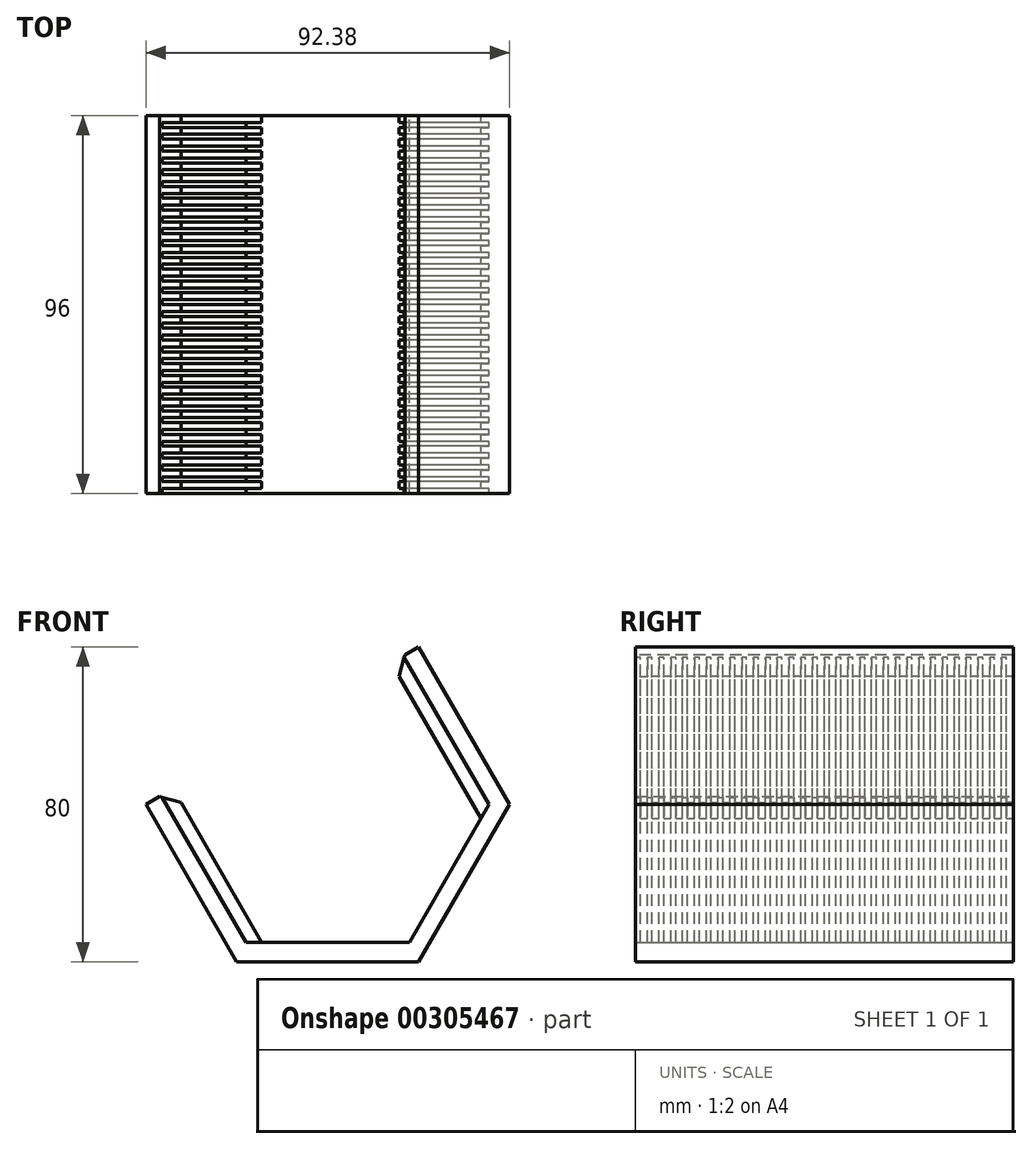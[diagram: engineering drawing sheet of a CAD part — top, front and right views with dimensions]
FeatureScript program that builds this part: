
annotation { "Feature Type Name" : "Feature", "Feature Type Description" : "" }
export const myFeature = defineFeature(function(context is Context, id is Id, definition is map)
    precondition{}
    {
        {
            var Q0;
            Q0=qCreatedBy(makeId("Front.planeOp"),FACE);
            var sketch = newSketch(context, id + "F0", { "sketchPlane" : qUnion([Q0])});
            skCircle(sketch, "E0.cCircle", {"center": v(0, 0) * mm, "radius": 46.19 * mm, "construction": true});
            skLineSegment(sketch, "E0.0", {"start": v(46.19, 0) * mm, "end": v(23.1, -40) * mm});
            skLineSegment(sketch, "E0.1", {"start": v(23.1, -40) * mm, "end": v(-23.1, -40) * mm});
            skLineSegment(sketch, "E0.2", {"start": v(-23.1, -40) * mm, "end": v(-46.19, 0) * mm});
            skLineSegment(sketch, "E0.3", {"start": v(-46.19, 0) * mm, "end": v(-23.1, 40) * mm});
            skLineSegment(sketch, "E0.4", {"start": v(-23.1, 40) * mm, "end": v(23.1, 40) * mm});
            skLineSegment(sketch, "E0.5", {"start": v(23.1, 40) * mm, "end": v(46.19, 0) * mm});
            skLineSegment(sketch, "E1.0", {"start": v(-21.36, -35) * mm, "end": v(-42.72, 2) * mm});
            skLineSegment(sketch, "E1.1", {"start": v(20.78, -35) * mm, "end": v(-21.36, -35) * mm});
            skLineSegment(sketch, "E1.2", {"start": v(41.28, 0.5) * mm, "end": v(20.78, -35) * mm});
            skLineSegment(sketch, "E1.3", {"start": v(19.63, 38) * mm, "end": v(41.28, 0.5) * mm});
            skLineSegment(sketch, "E2", {"start": v(-42.72, 2) * mm, "end": v(-46.19, 0) * mm});
            skLineSegment(sketch, "E3", {"start": v(19.63, 38) * mm, "end": v(23.1, 40) * mm});
            skSolve(sketch);
        }
        {
            var Q0;
            Q0=makeQuery(id+"F0.imprint","IMPRINT",FACE,{"disambiguationData":[TD([[makeQuery(id+"F0.imprint","IMPRINT",EDGE,{"derivedFrom":sQuery(id+"F0.wireOp",EDGE,"E0.0")}),-1.0]])]});
            extrude(context, id + "F1", {"entities" : qUnion([Q0]), "endBound" : BoundingType.SYMMETRIC, "depth" : 96 * mm});
        }
        {
            var Q0;
            Q0=makeQuery(id+"F1.opExtrude","SWEPT_FACE",FACE,{"disambiguationData":[OSD([sQuery(id+"F0.wireOp",EDGE,"E2")])]});
            var sketch = newSketch(context, id + "F2", { "sketchPlane" : qUnion([Q0])});
            skLineSegment(sketch, "E4", {"start": v(-32, 48) * mm, "end": v(-32, 46.25) * mm});
            skLineSegment(sketch, "E5", {"start": v(-32, 46.25) * mm, "end": v(-35.5, 46.25) * mm});
            skLineSegment(sketch, "E6", {"start": v(-35.5, 46.25) * mm, "end": v(-35.5, 45) * mm});
            skLineSegment(sketch, "E7", {"start": v(-36, 48) * mm, "end": v(-35.5, 48) * mm});
            skLineSegment(sketch, "E8", {"start": v(-35.5, 48) * mm, "end": v(-32, 48) * mm});
            skLineSegment(sketch, "E9.0.1.0", {"start": v(-35.5, 45) * mm, "end": v(-32, 45) * mm});
            skLineSegment(sketch, "E9.0.1.1", {"start": v(-32, 45) * mm, "end": v(-32, 43.25) * mm});
            skLineSegment(sketch, "E9.0.1.2", {"start": v(-32, 43.25) * mm, "end": v(-35.5, 43.25) * mm});
            skLineSegment(sketch, "E9.0.1.3", {"start": v(-35.5, 43.25) * mm, "end": v(-35.5, 42) * mm});
            skLineSegment(sketch, "E9.0.2.0", {"start": v(-35.5, 42) * mm, "end": v(-32, 42) * mm});
            skLineSegment(sketch, "E9.0.2.1", {"start": v(-32, 42) * mm, "end": v(-32, 40.25) * mm});
            skLineSegment(sketch, "E9.0.2.2", {"start": v(-32, 40.25) * mm, "end": v(-35.5, 40.25) * mm});
            skLineSegment(sketch, "E9.0.2.3", {"start": v(-35.5, 40.25) * mm, "end": v(-35.5, 39) * mm});
            skLineSegment(sketch, "E9.0.3.0", {"start": v(-35.5, 39) * mm, "end": v(-32, 39) * mm});
            skLineSegment(sketch, "E9.0.3.1", {"start": v(-32, 39) * mm, "end": v(-32, 37.25) * mm});
            skLineSegment(sketch, "E9.0.3.2", {"start": v(-32, 37.25) * mm, "end": v(-35.5, 37.25) * mm});
            skLineSegment(sketch, "E9.0.3.3", {"start": v(-35.5, 37.25) * mm, "end": v(-35.5, 36) * mm});
            skLineSegment(sketch, "E9.0.4.0", {"start": v(-35.5, 36) * mm, "end": v(-32, 36) * mm});
            skLineSegment(sketch, "E9.0.4.1", {"start": v(-32, 36) * mm, "end": v(-32, 34.25) * mm});
            skLineSegment(sketch, "E9.0.4.2", {"start": v(-32, 34.25) * mm, "end": v(-35.5, 34.25) * mm});
            skLineSegment(sketch, "E9.0.4.3", {"start": v(-35.5, 34.25) * mm, "end": v(-35.5, 33) * mm});
            skLineSegment(sketch, "E9.0.5.0", {"start": v(-35.5, 33) * mm, "end": v(-32, 33) * mm});
            skLineSegment(sketch, "E9.0.5.1", {"start": v(-32, 33) * mm, "end": v(-32, 31.25) * mm});
            skLineSegment(sketch, "E9.0.5.2", {"start": v(-32, 31.25) * mm, "end": v(-35.5, 31.25) * mm});
            skLineSegment(sketch, "E9.0.5.3", {"start": v(-35.5, 31.25) * mm, "end": v(-35.5, 30) * mm});
            skLineSegment(sketch, "E9.0.6.0", {"start": v(-35.5, 30) * mm, "end": v(-32, 30) * mm});
            skLineSegment(sketch, "E9.0.6.1", {"start": v(-32, 30) * mm, "end": v(-32, 28.25) * mm});
            skLineSegment(sketch, "E9.0.6.2", {"start": v(-32, 28.25) * mm, "end": v(-35.5, 28.25) * mm});
            skLineSegment(sketch, "E9.0.6.3", {"start": v(-35.5, 28.25) * mm, "end": v(-35.5, 27) * mm});
            skLineSegment(sketch, "E9.0.7.0", {"start": v(-35.5, 27) * mm, "end": v(-32, 27) * mm});
            skLineSegment(sketch, "E9.0.7.1", {"start": v(-32, 27) * mm, "end": v(-32, 25.25) * mm});
            skLineSegment(sketch, "E9.0.7.2", {"start": v(-32, 25.25) * mm, "end": v(-35.5, 25.25) * mm});
            skLineSegment(sketch, "E9.0.7.3", {"start": v(-35.5, 25.25) * mm, "end": v(-35.5, 24) * mm});
            skLineSegment(sketch, "E9.0.8.0", {"start": v(-35.5, 24) * mm, "end": v(-32, 24) * mm});
            skLineSegment(sketch, "E9.0.8.1", {"start": v(-32, 24) * mm, "end": v(-32, 22.25) * mm});
            skLineSegment(sketch, "E9.0.8.2", {"start": v(-32, 22.25) * mm, "end": v(-35.5, 22.25) * mm});
            skLineSegment(sketch, "E9.0.8.3", {"start": v(-35.5, 22.25) * mm, "end": v(-35.5, 21) * mm});
            skLineSegment(sketch, "E9.0.9.0", {"start": v(-35.5, 21) * mm, "end": v(-32, 21) * mm});
            skLineSegment(sketch, "E9.0.9.1", {"start": v(-32, 21) * mm, "end": v(-32, 19.25) * mm});
            skLineSegment(sketch, "E9.0.9.2", {"start": v(-32, 19.25) * mm, "end": v(-35.5, 19.25) * mm});
            skLineSegment(sketch, "E9.0.9.3", {"start": v(-35.5, 19.25) * mm, "end": v(-35.5, 18) * mm});
            skLineSegment(sketch, "E9.0.10.0", {"start": v(-35.5, 18) * mm, "end": v(-32, 18) * mm});
            skLineSegment(sketch, "E9.0.10.1", {"start": v(-32, 18) * mm, "end": v(-32, 16.25) * mm});
            skLineSegment(sketch, "E9.0.10.2", {"start": v(-32, 16.25) * mm, "end": v(-35.5, 16.25) * mm});
            skLineSegment(sketch, "E9.0.10.3", {"start": v(-35.5, 16.25) * mm, "end": v(-35.5, 15) * mm});
            skLineSegment(sketch, "E9.0.11.0", {"start": v(-35.5, 15) * mm, "end": v(-32, 15) * mm});
            skLineSegment(sketch, "E9.0.11.1", {"start": v(-32, 15) * mm, "end": v(-32, 13.25) * mm});
            skLineSegment(sketch, "E9.0.11.2", {"start": v(-32, 13.25) * mm, "end": v(-35.5, 13.25) * mm});
            skLineSegment(sketch, "E9.0.11.3", {"start": v(-35.5, 13.25) * mm, "end": v(-35.5, 12) * mm});
            skLineSegment(sketch, "E9.0.12.0", {"start": v(-35.5, 12) * mm, "end": v(-32, 12) * mm});
            skLineSegment(sketch, "E9.0.12.1", {"start": v(-32, 12) * mm, "end": v(-32, 10.25) * mm});
            skLineSegment(sketch, "E9.0.12.2", {"start": v(-32, 10.25) * mm, "end": v(-35.5, 10.25) * mm});
            skLineSegment(sketch, "E9.0.12.3", {"start": v(-35.5, 10.25) * mm, "end": v(-35.5, 9) * mm});
            skLineSegment(sketch, "E9.0.13.0", {"start": v(-35.5, 9) * mm, "end": v(-32, 9) * mm});
            skLineSegment(sketch, "E9.0.13.1", {"start": v(-32, 9) * mm, "end": v(-32, 7.25) * mm});
            skLineSegment(sketch, "E9.0.13.2", {"start": v(-32, 7.25) * mm, "end": v(-35.5, 7.25) * mm});
            skLineSegment(sketch, "E9.0.13.3", {"start": v(-35.5, 7.25) * mm, "end": v(-35.5, 6) * mm});
            skLineSegment(sketch, "E9.0.14.0", {"start": v(-35.5, 6) * mm, "end": v(-32, 6) * mm});
            skLineSegment(sketch, "E9.0.14.1", {"start": v(-32, 6) * mm, "end": v(-32, 4.25) * mm});
            skLineSegment(sketch, "E9.0.14.2", {"start": v(-32, 4.25) * mm, "end": v(-35.5, 4.25) * mm});
            skLineSegment(sketch, "E9.0.14.3", {"start": v(-35.5, 4.25) * mm, "end": v(-35.5, 3) * mm});
            skLineSegment(sketch, "E9.0.15.0", {"start": v(-35.5, 3) * mm, "end": v(-32, 3) * mm});
            skLineSegment(sketch, "E9.0.15.1", {"start": v(-32, 3) * mm, "end": v(-32, 1.25) * mm});
            skLineSegment(sketch, "E9.0.15.2", {"start": v(-32, 1.25) * mm, "end": v(-35.5, 1.25) * mm});
            skLineSegment(sketch, "E9.0.15.3", {"start": v(-35.5, 1.25) * mm, "end": v(-35.5, 0) * mm});
            skLineSegment(sketch, "E9.0.16.0", {"start": v(-35.5, 0) * mm, "end": v(-32, 0) * mm});
            skLineSegment(sketch, "E9.0.16.1", {"start": v(-32, 0) * mm, "end": v(-32, -1.75) * mm});
            skLineSegment(sketch, "E9.0.16.2", {"start": v(-32, -1.75) * mm, "end": v(-35.5, -1.75) * mm});
            skLineSegment(sketch, "E9.0.16.3", {"start": v(-35.5, -1.75) * mm, "end": v(-35.5, -3) * mm});
            skLineSegment(sketch, "E9.0.17.0", {"start": v(-35.5, -3) * mm, "end": v(-32, -3) * mm});
            skLineSegment(sketch, "E9.0.17.1", {"start": v(-32, -3) * mm, "end": v(-32, -4.75) * mm});
            skLineSegment(sketch, "E9.0.17.2", {"start": v(-32, -4.75) * mm, "end": v(-35.5, -4.75) * mm});
            skLineSegment(sketch, "E9.0.17.3", {"start": v(-35.5, -4.75) * mm, "end": v(-35.5, -6) * mm});
            skLineSegment(sketch, "E9.0.18.0", {"start": v(-35.5, -6) * mm, "end": v(-32, -6) * mm});
            skLineSegment(sketch, "E9.0.18.1", {"start": v(-32, -6) * mm, "end": v(-32, -7.75) * mm});
            skLineSegment(sketch, "E9.0.18.2", {"start": v(-32, -7.75) * mm, "end": v(-35.5, -7.75) * mm});
            skLineSegment(sketch, "E9.0.18.3", {"start": v(-35.5, -7.75) * mm, "end": v(-35.5, -9) * mm});
            skLineSegment(sketch, "E9.0.19.0", {"start": v(-35.5, -9) * mm, "end": v(-32, -9) * mm});
            skLineSegment(sketch, "E9.0.19.1", {"start": v(-32, -9) * mm, "end": v(-32, -10.75) * mm});
            skLineSegment(sketch, "E9.0.19.2", {"start": v(-32, -10.75) * mm, "end": v(-35.5, -10.75) * mm});
            skLineSegment(sketch, "E9.0.19.3", {"start": v(-35.5, -10.75) * mm, "end": v(-35.5, -12) * mm});
            skLineSegment(sketch, "E9.direction1", {"start": v(-35.5, 48) * mm, "end": v(-25.3, 48) * mm, "construction": true});
            skLineSegment(sketch, "E9.direction2", {"start": v(-35.5, 48) * mm, "end": v(-35.5, 45) * mm, "construction": true});
            skLineSegment(sketch, "E10.0.0.20", {"start": v(-35.5, -12) * mm, "end": v(-32, -12) * mm});
            skLineSegment(sketch, "E10.3.0.20", {"start": v(-32, -12) * mm, "end": v(-32, -13.75) * mm});
            skLineSegment(sketch, "E10.6.0.20", {"start": v(-32, -13.75) * mm, "end": v(-35.5, -13.75) * mm});
            skLineSegment(sketch, "E10.9.0.20", {"start": v(-35.5, -13.75) * mm, "end": v(-35.5, -15) * mm});
            skLineSegment(sketch, "E10.0.0.21", {"start": v(-35.5, -15) * mm, "end": v(-32, -15) * mm});
            skLineSegment(sketch, "E10.3.0.21", {"start": v(-32, -15) * mm, "end": v(-32, -16.75) * mm});
            skLineSegment(sketch, "E10.6.0.21", {"start": v(-32, -16.75) * mm, "end": v(-35.5, -16.75) * mm});
            skLineSegment(sketch, "E10.9.0.21", {"start": v(-35.5, -16.75) * mm, "end": v(-35.5, -18) * mm});
            skLineSegment(sketch, "E10.0.0.22", {"start": v(-35.5, -18) * mm, "end": v(-32, -18) * mm});
            skLineSegment(sketch, "E10.3.0.22", {"start": v(-32, -18) * mm, "end": v(-32, -19.75) * mm});
            skLineSegment(sketch, "E10.6.0.22", {"start": v(-32, -19.75) * mm, "end": v(-35.5, -19.75) * mm});
            skLineSegment(sketch, "E10.9.0.22", {"start": v(-35.5, -19.75) * mm, "end": v(-35.5, -21) * mm});
            skLineSegment(sketch, "E10.0.0.23", {"start": v(-35.5, -21) * mm, "end": v(-32, -21) * mm});
            skLineSegment(sketch, "E10.3.0.23", {"start": v(-32, -21) * mm, "end": v(-32, -22.75) * mm});
            skLineSegment(sketch, "E10.6.0.23", {"start": v(-32, -22.75) * mm, "end": v(-35.5, -22.75) * mm});
            skLineSegment(sketch, "E10.9.0.23", {"start": v(-35.5, -22.75) * mm, "end": v(-35.5, -24) * mm});
            skLineSegment(sketch, "E10.0.0.24", {"start": v(-35.5, -24) * mm, "end": v(-32, -24) * mm});
            skLineSegment(sketch, "E10.3.0.24", {"start": v(-32, -24) * mm, "end": v(-32, -25.75) * mm});
            skLineSegment(sketch, "E10.6.0.24", {"start": v(-32, -25.75) * mm, "end": v(-35.5, -25.75) * mm});
            skLineSegment(sketch, "E10.9.0.24", {"start": v(-35.5, -25.75) * mm, "end": v(-35.5, -27) * mm});
            skLineSegment(sketch, "E10.0.0.25", {"start": v(-35.5, -27) * mm, "end": v(-32, -27) * mm});
            skLineSegment(sketch, "E10.3.0.25", {"start": v(-32, -27) * mm, "end": v(-32, -28.75) * mm});
            skLineSegment(sketch, "E10.6.0.25", {"start": v(-32, -28.75) * mm, "end": v(-35.5, -28.75) * mm});
            skLineSegment(sketch, "E10.9.0.25", {"start": v(-35.5, -28.75) * mm, "end": v(-35.5, -30) * mm});
            skLineSegment(sketch, "E10.0.0.26", {"start": v(-35.5, -30) * mm, "end": v(-32, -30) * mm});
            skLineSegment(sketch, "E10.3.0.26", {"start": v(-32, -30) * mm, "end": v(-32, -31.75) * mm});
            skLineSegment(sketch, "E10.6.0.26", {"start": v(-32, -31.75) * mm, "end": v(-35.5, -31.75) * mm});
            skLineSegment(sketch, "E10.9.0.26", {"start": v(-35.5, -31.75) * mm, "end": v(-35.5, -33) * mm});
            skLineSegment(sketch, "E10.0.0.27", {"start": v(-35.5, -33) * mm, "end": v(-32, -33) * mm});
            skLineSegment(sketch, "E10.3.0.27", {"start": v(-32, -33) * mm, "end": v(-32, -34.75) * mm});
            skLineSegment(sketch, "E10.6.0.27", {"start": v(-32, -34.75) * mm, "end": v(-35.5, -34.75) * mm});
            skLineSegment(sketch, "E10.9.0.27", {"start": v(-35.5, -34.75) * mm, "end": v(-35.5, -36) * mm});
            skLineSegment(sketch, "E10.0.0.28", {"start": v(-35.5, -36) * mm, "end": v(-32, -36) * mm});
            skLineSegment(sketch, "E10.3.0.28", {"start": v(-32, -36) * mm, "end": v(-32, -37.75) * mm});
            skLineSegment(sketch, "E10.6.0.28", {"start": v(-32, -37.75) * mm, "end": v(-35.5, -37.75) * mm});
            skLineSegment(sketch, "E10.9.0.28", {"start": v(-35.5, -37.75) * mm, "end": v(-35.5, -39) * mm});
            skLineSegment(sketch, "E10.0.0.29", {"start": v(-35.5, -39) * mm, "end": v(-32, -39) * mm});
            skLineSegment(sketch, "E10.3.0.29", {"start": v(-32, -39) * mm, "end": v(-32, -40.75) * mm});
            skLineSegment(sketch, "E10.6.0.29", {"start": v(-32, -40.75) * mm, "end": v(-35.5, -40.75) * mm});
            skLineSegment(sketch, "E10.9.0.29", {"start": v(-35.5, -40.75) * mm, "end": v(-35.5, -42) * mm});
            skLineSegment(sketch, "E11.0.0.30", {"start": v(-35.5, -42) * mm, "end": v(-32, -42) * mm});
            skLineSegment(sketch, "E11.3.0.30", {"start": v(-32, -42) * mm, "end": v(-32, -43.75) * mm});
            skLineSegment(sketch, "E11.6.0.30", {"start": v(-32, -43.75) * mm, "end": v(-35.5, -43.75) * mm});
            skLineSegment(sketch, "E11.9.0.30", {"start": v(-35.5, -43.75) * mm, "end": v(-35.5, -45) * mm});
            skLineSegment(sketch, "E11.0.0.31", {"start": v(-35.5, -45) * mm, "end": v(-32, -45) * mm});
            skLineSegment(sketch, "E11.3.0.31", {"start": v(-32, -45) * mm, "end": v(-32, -46.75) * mm});
            skLineSegment(sketch, "E11.6.0.31", {"start": v(-32, -46.75) * mm, "end": v(-35.5, -46.75) * mm});
            skLineSegment(sketch, "E11.9.0.31", {"start": v(-35.5, -46.75) * mm, "end": v(-35.5, -48) * mm});
            skLineSegment(sketch, "E12", {"start": v(-35.5, -48) * mm, "end": v(-36, -48) * mm});
            skSolve(sketch);
        }
        {
            var Q0;
            Q0 = qSketchRegion(id + "F2", true);
            var Q1;
            Q1=makeQuery(id+"F2.imprint","IMPRINT",FACE,{"disambiguationData":[TD([[makeQuery(id+"F2.imprint","IMPRINT",EDGE,{"derivedFrom":sQuery(id+"F2.wireOp",EDGE,"E4")}),-1.0]])]});
            extrude(context, id + "F3", {"entities" : qUnion([Q0, Q1]), "operationType" : NewBodyOperationType.ADD, "oppositeDirection" : true, "depth" : 46 * mm});
        }
        {
            var Q0;
            Q0=makeQuery(id+"F1.opExtrude","SWEPT_FACE",FACE,{"disambiguationData":[OSD([sQuery(id+"F0.wireOp",EDGE,"E3")])]});
            var sketch = newSketch(context, id + "F4", { "sketchPlane" : qUnion([Q0])});
            skLineSegment(sketch, "E13", {"start": v(36, 48) * mm, "end": v(35.5, 48) * mm});
            skLineSegment(sketch, "E14", {"start": v(35.5, 48) * mm, "end": v(32, 48) * mm});
            skLineSegment(sketch, "E15", {"start": v(32, 48) * mm, "end": v(32, 46.25) * mm});
            skLineSegment(sketch, "E16", {"start": v(32, 46.25) * mm, "end": v(35.5, 46.25) * mm});
            skLineSegment(sketch, "E17", {"start": v(35.5, 46.25) * mm, "end": v(35.5, 45) * mm});
            skLineSegment(sketch, "E18.0.1.0", {"start": v(35.5, 45) * mm, "end": v(32, 45) * mm});
            skLineSegment(sketch, "E18.0.1.1", {"start": v(32, 45) * mm, "end": v(32, 43.25) * mm});
            skLineSegment(sketch, "E18.0.1.2", {"start": v(32, 43.25) * mm, "end": v(35.5, 43.25) * mm});
            skLineSegment(sketch, "E18.0.1.3", {"start": v(35.5, 43.25) * mm, "end": v(35.5, 42) * mm});
            skLineSegment(sketch, "E18.0.2.0", {"start": v(35.5, 42) * mm, "end": v(32, 42) * mm});
            skLineSegment(sketch, "E18.0.2.1", {"start": v(32, 42) * mm, "end": v(32, 40.25) * mm});
            skLineSegment(sketch, "E18.0.2.2", {"start": v(32, 40.25) * mm, "end": v(35.5, 40.25) * mm});
            skLineSegment(sketch, "E18.0.2.3", {"start": v(35.5, 40.25) * mm, "end": v(35.5, 39) * mm});
            skLineSegment(sketch, "E18.0.3.0", {"start": v(35.5, 39) * mm, "end": v(32, 39) * mm});
            skLineSegment(sketch, "E18.0.3.1", {"start": v(32, 39) * mm, "end": v(32, 37.25) * mm});
            skLineSegment(sketch, "E18.0.3.2", {"start": v(32, 37.25) * mm, "end": v(35.5, 37.25) * mm});
            skLineSegment(sketch, "E18.0.3.3", {"start": v(35.5, 37.25) * mm, "end": v(35.5, 36) * mm});
            skLineSegment(sketch, "E18.0.4.0", {"start": v(35.5, 36) * mm, "end": v(32, 36) * mm});
            skLineSegment(sketch, "E18.0.4.1", {"start": v(32, 36) * mm, "end": v(32, 34.25) * mm});
            skLineSegment(sketch, "E18.0.4.2", {"start": v(32, 34.25) * mm, "end": v(35.5, 34.25) * mm});
            skLineSegment(sketch, "E18.0.4.3", {"start": v(35.5, 34.25) * mm, "end": v(35.5, 33) * mm});
            skLineSegment(sketch, "E18.0.5.0", {"start": v(35.5, 33) * mm, "end": v(32, 33) * mm});
            skLineSegment(sketch, "E18.0.5.1", {"start": v(32, 33) * mm, "end": v(32, 31.25) * mm});
            skLineSegment(sketch, "E18.0.5.2", {"start": v(32, 31.25) * mm, "end": v(35.5, 31.25) * mm});
            skLineSegment(sketch, "E18.0.5.3", {"start": v(35.5, 31.25) * mm, "end": v(35.5, 30) * mm});
            skLineSegment(sketch, "E18.0.6.0", {"start": v(35.5, 30) * mm, "end": v(32, 30) * mm});
            skLineSegment(sketch, "E18.0.6.1", {"start": v(32, 30) * mm, "end": v(32, 28.25) * mm});
            skLineSegment(sketch, "E18.0.6.2", {"start": v(32, 28.25) * mm, "end": v(35.5, 28.25) * mm});
            skLineSegment(sketch, "E18.0.6.3", {"start": v(35.5, 28.25) * mm, "end": v(35.5, 27) * mm});
            skLineSegment(sketch, "E18.0.7.0", {"start": v(35.5, 27) * mm, "end": v(32, 27) * mm});
            skLineSegment(sketch, "E18.0.7.1", {"start": v(32, 27) * mm, "end": v(32, 25.25) * mm});
            skLineSegment(sketch, "E18.0.7.2", {"start": v(32, 25.25) * mm, "end": v(35.5, 25.25) * mm});
            skLineSegment(sketch, "E18.0.7.3", {"start": v(35.5, 25.25) * mm, "end": v(35.5, 24) * mm});
            skLineSegment(sketch, "E18.0.8.0", {"start": v(35.5, 24) * mm, "end": v(32, 24) * mm});
            skLineSegment(sketch, "E18.0.8.1", {"start": v(32, 24) * mm, "end": v(32, 22.25) * mm});
            skLineSegment(sketch, "E18.0.8.2", {"start": v(32, 22.25) * mm, "end": v(35.5, 22.25) * mm});
            skLineSegment(sketch, "E18.0.8.3", {"start": v(35.5, 22.25) * mm, "end": v(35.5, 21) * mm});
            skLineSegment(sketch, "E18.0.9.0", {"start": v(35.5, 21) * mm, "end": v(32, 21) * mm});
            skLineSegment(sketch, "E18.0.9.1", {"start": v(32, 21) * mm, "end": v(32, 19.25) * mm});
            skLineSegment(sketch, "E18.0.9.2", {"start": v(32, 19.25) * mm, "end": v(35.5, 19.25) * mm});
            skLineSegment(sketch, "E18.0.9.3", {"start": v(35.5, 19.25) * mm, "end": v(35.5, 18) * mm});
            skLineSegment(sketch, "E18.0.10.0", {"start": v(35.5, 18) * mm, "end": v(32, 18) * mm});
            skLineSegment(sketch, "E18.0.10.1", {"start": v(32, 18) * mm, "end": v(32, 16.25) * mm});
            skLineSegment(sketch, "E18.0.10.2", {"start": v(32, 16.25) * mm, "end": v(35.5, 16.25) * mm});
            skLineSegment(sketch, "E18.0.10.3", {"start": v(35.5, 16.25) * mm, "end": v(35.5, 15) * mm});
            skLineSegment(sketch, "E18.0.11.0", {"start": v(35.5, 15) * mm, "end": v(32, 15) * mm});
            skLineSegment(sketch, "E18.0.11.1", {"start": v(32, 15) * mm, "end": v(32, 13.25) * mm});
            skLineSegment(sketch, "E18.0.11.2", {"start": v(32, 13.25) * mm, "end": v(35.5, 13.25) * mm});
            skLineSegment(sketch, "E18.0.11.3", {"start": v(35.5, 13.25) * mm, "end": v(35.5, 12) * mm});
            skLineSegment(sketch, "E18.0.12.0", {"start": v(35.5, 12) * mm, "end": v(32, 12) * mm});
            skLineSegment(sketch, "E18.0.12.1", {"start": v(32, 12) * mm, "end": v(32, 10.25) * mm});
            skLineSegment(sketch, "E18.0.12.2", {"start": v(32, 10.25) * mm, "end": v(35.5, 10.25) * mm});
            skLineSegment(sketch, "E18.0.12.3", {"start": v(35.5, 10.25) * mm, "end": v(35.5, 9) * mm});
            skLineSegment(sketch, "E18.0.13.0", {"start": v(35.5, 9) * mm, "end": v(32, 9) * mm});
            skLineSegment(sketch, "E18.0.13.1", {"start": v(32, 9) * mm, "end": v(32, 7.25) * mm});
            skLineSegment(sketch, "E18.0.13.2", {"start": v(32, 7.25) * mm, "end": v(35.5, 7.25) * mm});
            skLineSegment(sketch, "E18.0.13.3", {"start": v(35.5, 7.25) * mm, "end": v(35.5, 6) * mm});
            skLineSegment(sketch, "E18.0.14.0", {"start": v(35.5, 6) * mm, "end": v(32, 6) * mm});
            skLineSegment(sketch, "E18.0.14.1", {"start": v(32, 6) * mm, "end": v(32, 4.25) * mm});
            skLineSegment(sketch, "E18.0.14.2", {"start": v(32, 4.25) * mm, "end": v(35.5, 4.25) * mm});
            skLineSegment(sketch, "E18.0.14.3", {"start": v(35.5, 4.25) * mm, "end": v(35.5, 3) * mm});
            skLineSegment(sketch, "E18.0.15.0", {"start": v(35.5, 3) * mm, "end": v(32, 3) * mm});
            skLineSegment(sketch, "E18.0.15.1", {"start": v(32, 3) * mm, "end": v(32, 1.25) * mm});
            skLineSegment(sketch, "E18.0.15.2", {"start": v(32, 1.25) * mm, "end": v(35.5, 1.25) * mm});
            skLineSegment(sketch, "E18.0.15.3", {"start": v(35.5, 1.25) * mm, "end": v(35.5, 0) * mm});
            skLineSegment(sketch, "E18.0.16.0", {"start": v(35.5, 0) * mm, "end": v(32, 0) * mm});
            skLineSegment(sketch, "E18.0.16.1", {"start": v(32, 0) * mm, "end": v(32, -1.75) * mm});
            skLineSegment(sketch, "E18.0.16.2", {"start": v(32, -1.75) * mm, "end": v(35.5, -1.75) * mm});
            skLineSegment(sketch, "E18.0.16.3", {"start": v(35.5, -1.75) * mm, "end": v(35.5, -3) * mm});
            skLineSegment(sketch, "E18.0.17.0", {"start": v(35.5, -3) * mm, "end": v(32, -3) * mm});
            skLineSegment(sketch, "E18.0.17.1", {"start": v(32, -3) * mm, "end": v(32, -4.75) * mm});
            skLineSegment(sketch, "E18.0.17.2", {"start": v(32, -4.75) * mm, "end": v(35.5, -4.75) * mm});
            skLineSegment(sketch, "E18.0.17.3", {"start": v(35.5, -4.75) * mm, "end": v(35.5, -6) * mm});
            skLineSegment(sketch, "E18.0.18.0", {"start": v(35.5, -6) * mm, "end": v(32, -6) * mm});
            skLineSegment(sketch, "E18.0.18.1", {"start": v(32, -6) * mm, "end": v(32, -7.75) * mm});
            skLineSegment(sketch, "E18.0.18.2", {"start": v(32, -7.75) * mm, "end": v(35.5, -7.75) * mm});
            skLineSegment(sketch, "E18.0.18.3", {"start": v(35.5, -7.75) * mm, "end": v(35.5, -9) * mm});
            skLineSegment(sketch, "E18.0.19.0", {"start": v(35.5, -9) * mm, "end": v(32, -9) * mm});
            skLineSegment(sketch, "E18.0.19.1", {"start": v(32, -9) * mm, "end": v(32, -10.75) * mm});
            skLineSegment(sketch, "E18.0.19.2", {"start": v(32, -10.75) * mm, "end": v(35.5, -10.75) * mm});
            skLineSegment(sketch, "E18.0.19.3", {"start": v(35.5, -10.75) * mm, "end": v(35.5, -12) * mm});
            skLineSegment(sketch, "E18.0.20.0", {"start": v(35.5, -12) * mm, "end": v(32, -12) * mm});
            skLineSegment(sketch, "E18.0.20.1", {"start": v(32, -12) * mm, "end": v(32, -13.75) * mm});
            skLineSegment(sketch, "E18.0.20.2", {"start": v(32, -13.75) * mm, "end": v(35.5, -13.75) * mm});
            skLineSegment(sketch, "E18.0.20.3", {"start": v(35.5, -13.75) * mm, "end": v(35.5, -15) * mm});
            skLineSegment(sketch, "E18.0.21.0", {"start": v(35.5, -15) * mm, "end": v(32, -15) * mm});
            skLineSegment(sketch, "E18.0.21.1", {"start": v(32, -15) * mm, "end": v(32, -16.75) * mm});
            skLineSegment(sketch, "E18.0.21.2", {"start": v(32, -16.75) * mm, "end": v(35.5, -16.75) * mm});
            skLineSegment(sketch, "E18.0.21.3", {"start": v(35.5, -16.75) * mm, "end": v(35.5, -18) * mm});
            skLineSegment(sketch, "E18.0.22.0", {"start": v(35.5, -18) * mm, "end": v(32, -18) * mm});
            skLineSegment(sketch, "E18.0.22.1", {"start": v(32, -18) * mm, "end": v(32, -19.75) * mm});
            skLineSegment(sketch, "E18.0.22.2", {"start": v(32, -19.75) * mm, "end": v(35.5, -19.75) * mm});
            skLineSegment(sketch, "E18.0.22.3", {"start": v(35.5, -19.75) * mm, "end": v(35.5, -21) * mm});
            skLineSegment(sketch, "E18.0.23.0", {"start": v(35.5, -21) * mm, "end": v(32, -21) * mm});
            skLineSegment(sketch, "E18.0.23.1", {"start": v(32, -21) * mm, "end": v(32, -22.75) * mm});
            skLineSegment(sketch, "E18.0.23.2", {"start": v(32, -22.75) * mm, "end": v(35.5, -22.75) * mm});
            skLineSegment(sketch, "E18.0.23.3", {"start": v(35.5, -22.75) * mm, "end": v(35.5, -24) * mm});
            skLineSegment(sketch, "E18.0.24.0", {"start": v(35.5, -24) * mm, "end": v(32, -24) * mm});
            skLineSegment(sketch, "E18.0.24.1", {"start": v(32, -24) * mm, "end": v(32, -25.75) * mm});
            skLineSegment(sketch, "E18.0.24.2", {"start": v(32, -25.75) * mm, "end": v(35.5, -25.75) * mm});
            skLineSegment(sketch, "E18.0.24.3", {"start": v(35.5, -25.75) * mm, "end": v(35.5, -27) * mm});
            skLineSegment(sketch, "E18.0.25.0", {"start": v(35.5, -27) * mm, "end": v(32, -27) * mm});
            skLineSegment(sketch, "E18.0.25.1", {"start": v(32, -27) * mm, "end": v(32, -28.75) * mm});
            skLineSegment(sketch, "E18.0.25.2", {"start": v(32, -28.75) * mm, "end": v(35.5, -28.75) * mm});
            skLineSegment(sketch, "E18.0.25.3", {"start": v(35.5, -28.75) * mm, "end": v(35.5, -30) * mm});
            skLineSegment(sketch, "E18.0.26.0", {"start": v(35.5, -30) * mm, "end": v(32, -30) * mm});
            skLineSegment(sketch, "E18.0.26.1", {"start": v(32, -30) * mm, "end": v(32, -31.75) * mm});
            skLineSegment(sketch, "E18.0.26.2", {"start": v(32, -31.75) * mm, "end": v(35.5, -31.75) * mm});
            skLineSegment(sketch, "E18.0.26.3", {"start": v(35.5, -31.75) * mm, "end": v(35.5, -33) * mm});
            skLineSegment(sketch, "E18.0.27.0", {"start": v(35.5, -33) * mm, "end": v(32, -33) * mm});
            skLineSegment(sketch, "E18.0.27.1", {"start": v(32, -33) * mm, "end": v(32, -34.75) * mm});
            skLineSegment(sketch, "E18.0.27.2", {"start": v(32, -34.75) * mm, "end": v(35.5, -34.75) * mm});
            skLineSegment(sketch, "E18.0.27.3", {"start": v(35.5, -34.75) * mm, "end": v(35.5, -36) * mm});
            skLineSegment(sketch, "E18.0.28.0", {"start": v(35.5, -36) * mm, "end": v(32, -36) * mm});
            skLineSegment(sketch, "E18.0.28.1", {"start": v(32, -36) * mm, "end": v(32, -37.75) * mm});
            skLineSegment(sketch, "E18.0.28.2", {"start": v(32, -37.75) * mm, "end": v(35.5, -37.75) * mm});
            skLineSegment(sketch, "E18.0.28.3", {"start": v(35.5, -37.75) * mm, "end": v(35.5, -39) * mm});
            skLineSegment(sketch, "E18.0.29.0", {"start": v(35.5, -39) * mm, "end": v(32, -39) * mm});
            skLineSegment(sketch, "E18.0.29.1", {"start": v(32, -39) * mm, "end": v(32, -40.75) * mm});
            skLineSegment(sketch, "E18.0.29.2", {"start": v(32, -40.75) * mm, "end": v(35.5, -40.75) * mm});
            skLineSegment(sketch, "E18.0.29.3", {"start": v(35.5, -40.75) * mm, "end": v(35.5, -42) * mm});
            skLineSegment(sketch, "E18.0.30.0", {"start": v(35.5, -42) * mm, "end": v(32, -42) * mm});
            skLineSegment(sketch, "E18.0.30.1", {"start": v(32, -42) * mm, "end": v(32, -43.75) * mm});
            skLineSegment(sketch, "E18.0.30.2", {"start": v(32, -43.75) * mm, "end": v(35.5, -43.75) * mm});
            skLineSegment(sketch, "E18.0.30.3", {"start": v(35.5, -43.75) * mm, "end": v(35.5, -45) * mm});
            skLineSegment(sketch, "E18.0.31.0", {"start": v(35.5, -45) * mm, "end": v(32, -45) * mm});
            skLineSegment(sketch, "E18.0.31.1", {"start": v(32, -45) * mm, "end": v(32, -46.75) * mm});
            skLineSegment(sketch, "E18.0.31.2", {"start": v(32, -46.75) * mm, "end": v(35.5, -46.75) * mm});
            skLineSegment(sketch, "E18.0.31.3", {"start": v(35.5, -46.75) * mm, "end": v(35.5, -48) * mm});
            skLineSegment(sketch, "E18.direction1", {"start": v(32, 48) * mm, "end": v(58, 48) * mm, "construction": true});
            skLineSegment(sketch, "E18.direction2", {"start": v(32, 48) * mm, "end": v(32, 45) * mm, "construction": true});
            skLineSegment(sketch, "E19", {"start": v(36, -48) * mm, "end": v(35.5, -48) * mm});
            skSolve(sketch);
        }
        {
            var Q0;
            Q0=makeQuery(id+"F4.imprint","IMPRINT",FACE,{"disambiguationData":[TD([[makeQuery(id+"F4.imprint","IMPRINT",EDGE,{"derivedFrom":sQuery(id+"F4.wireOp",EDGE,"E13")}),1.0]])]});
            extrude(context, id + "F5", {"entities" : qUnion([Q0]), "operationType" : NewBodyOperationType.ADD, "oppositeDirection" : true, "depth" : 46 * mm});
        }
        {
            var Q0;
            Q0=makeQuery(id+"F3.opExtrude","CAP_EDGE",EDGE,{"disambiguationData":[OSD([sQuery(id+"F2.wireOp",EDGE,"E4")])],"isStart":true});
            var Q1;
            Q1=makeQuery(id+"F5.opExtrude","CAP_EDGE",EDGE,{"disambiguationData":[OSD([sQuery(id+"F4.wireOp",EDGE,"E18.0.31.1")])],"isStart":true});
            chamfer(context, id + "F6", {"entities" : qUnion([Q0, Q1]), "width" : 4 * mm, "tangentPropagation" : true});
        }
    });
